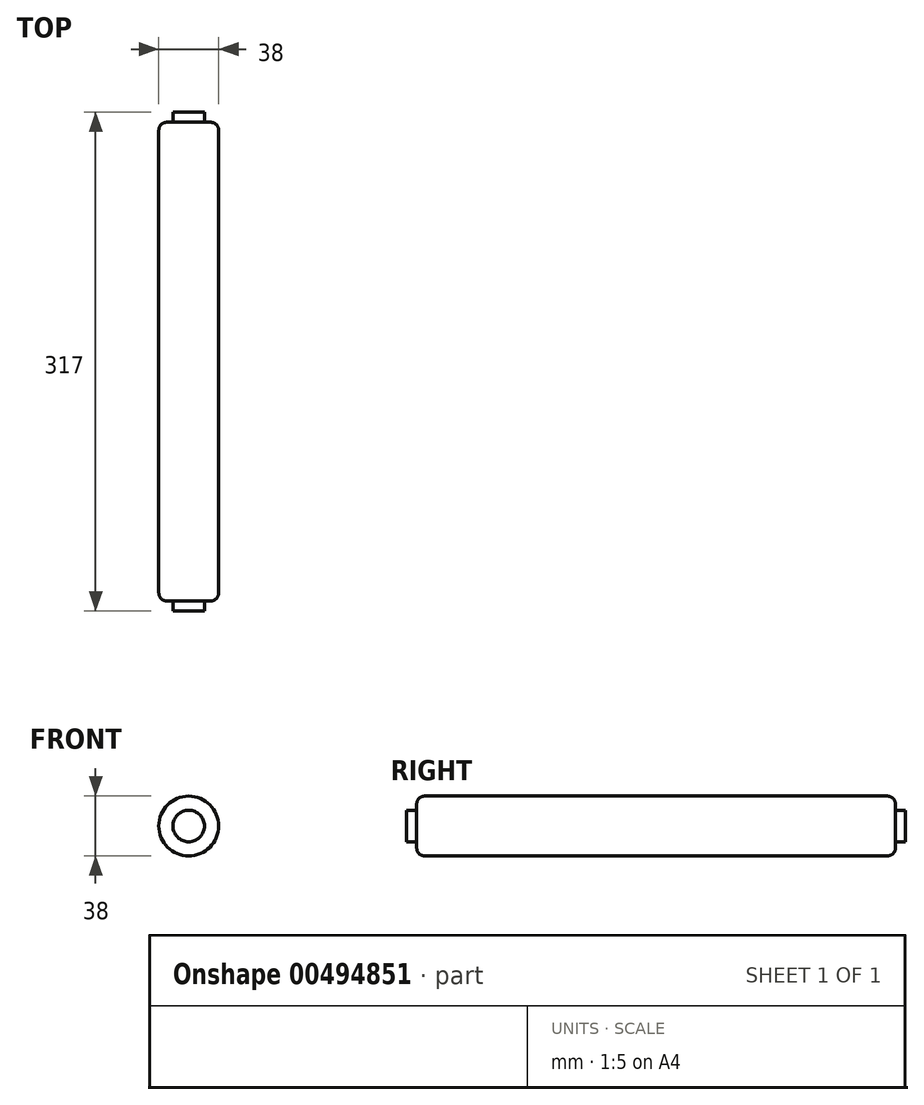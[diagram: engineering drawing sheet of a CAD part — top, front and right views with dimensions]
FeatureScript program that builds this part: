
annotation { "Feature Type Name" : "Feature", "Feature Type Description" : "" }
export const myFeature = defineFeature(function(context is Context, id is Id, definition is map)
    precondition{}
    {
        {
            var Q0;
            Q0=qCreatedBy(makeId("Front.planeOp"),FACE);
            var sketch = newSketch(context, id + "F0", { "sketchPlane" : qUnion([Q0])});
            skCircle(sketch, "E0", {"center": v(0, 0) * mm, "radius": 10 * mm});
            skSolve(sketch);
        }
        {
            var Q0;
            Q0=qSketchRegion(id+"F0",true);
            extrude(context, id + "F1", {"entities" : qUnion([Q0]), "depth" : 6.5 * mm});
        }
        {
            var Q0;
            Q0=qCreatedBy(makeId("Front.planeOp"),FACE);
            var sketch = newSketch(context, id + "F2", { "sketchPlane" : qUnion([Q0])});
            skCircle(sketch, "E1", {"center": v(0, 0) * mm, "radius": 19 * mm});
            skSolve(sketch);
        }
        {
            var Q0;
            Q0=qSketchRegion(id+"F2",true);
            extrude(context, id + "F3", {"entities" : qUnion([Q0]), "operationType" : NewBodyOperationType.ADD, "oppositeDirection" : true, "depth" : 304 * mm});
        }
        {
            var Q0;
            Q0=makeQuery(id+"F3.opExtrude","CAP_FACE",FACE,{"disambiguationData":[OSD([sQuery(id+"F2.wireOp",EDGE,"E1")])],"isStart":false});
            var sketch = newSketch(context, id + "F4", { "sketchPlane" : qUnion([Q0])});
            skCircle(sketch, "E2", {"center": v(0, 0) * mm, "radius": 10 * mm});
            skSolve(sketch);
        }
        {
            var Q0;
            Q0=qSketchRegion(id+"F4",true);
            extrude(context, id + "F5", {"entities" : qUnion([Q0]), "operationType" : NewBodyOperationType.ADD, "depth" : 6.5 * mm});
        }
        {
            var Q0;
            Q0=qCreatedBy(makeId("Front.planeOp"),FACE);
            var sketch = newSketch(context, id + "F6", { "sketchPlane" : qUnion([Q0])});
            skCircle(sketch, "E3", {"center": v(0, 0) * mm, "radius": 6 * mm});
            skSolve(sketch);
        }
        {
            var Q0;
            Q0=makeQuery(id+"F3.opExtrude","CAP_EDGE",EDGE,{"disambiguationData":[OSD([sQuery(id+"F2.wireOp",EDGE,"E1")])],"isStart":false});
            var Q1;
            Q1=makeQuery(id+"F3.opExtrude","CAP_EDGE",EDGE,{"disambiguationData":[OSD([sQuery(id+"F2.wireOp",EDGE,"E1")])],"isStart":true});
            fillet(context, id + "F7", {"entities" : qUnion([Q0, Q1]), "radius" : 5 * mm, "tangentPropagation" : true, "allowEdgeOverflow" : false});
        }
    });
